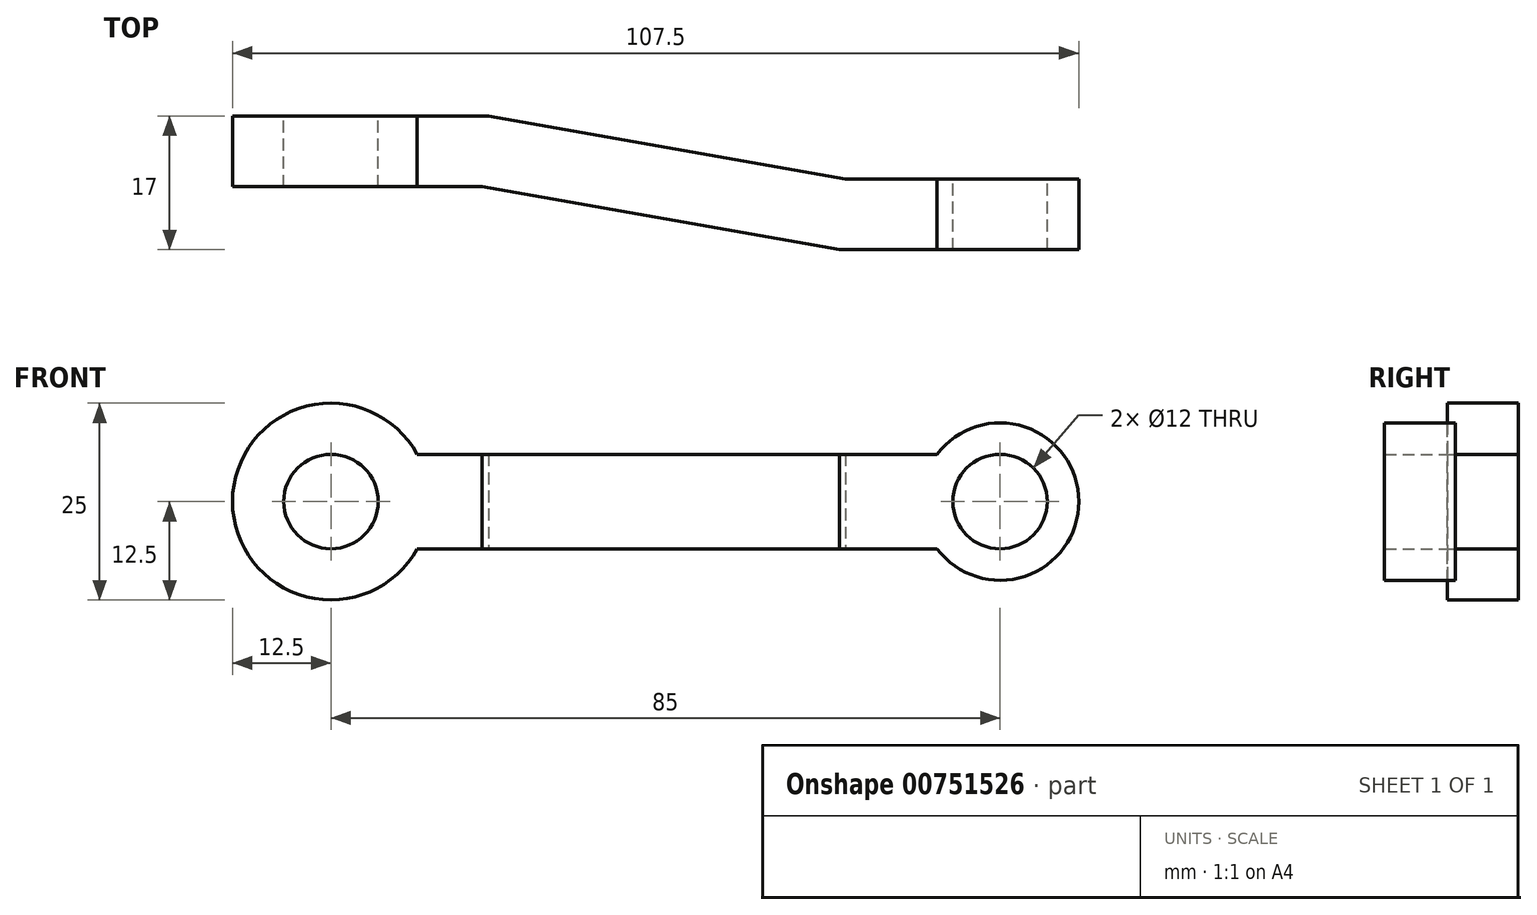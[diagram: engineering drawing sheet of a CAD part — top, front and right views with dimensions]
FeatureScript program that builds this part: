
annotation { "Feature Type Name" : "Feature", "Feature Type Description" : "" }
export const myFeature = defineFeature(function(context is Context, id is Id, definition is map)
    precondition{}
    {
        {
            var Q0;
            Q0=qCreatedBy(makeId("Front.planeOp"),FACE);
            var sketch = newSketch(context, id + "F0", { "sketchPlane" : qUnion([Q0])});
            skCircle(sketch, "E0", {"center": v(0, 0) * mm, "radius": 12.5 * mm});
            skCircle(sketch, "E1", {"center": v(85, 0) * mm, "radius": 10 * mm});
            skLineSegment(sketch, "E2", {"start": v(10.97, 6) * mm, "end": v(77, 6) * mm});
            skLineSegment(sketch, "E3", {"start": v(1.08, 0) * mm, "end": v(85, 0) * mm, "construction": true});
            skLineSegment(sketch, "E4.MirrorCS", {"start": v(10.97, -6) * mm, "end": v(77, -6) * mm});
            skCircle(sketch, "E5", {"center": v(0, 0) * mm, "radius": 6 * mm});
            skCircle(sketch, "E6", {"center": v(85, 0) * mm, "radius": 6 * mm});
            skSolve(sketch);
        }
        {
            var Q0;
            {var subQ0=sQuery(id+"F0.wireOp",EDGE,"E2");Q0=makeQuery(id+"F0.imprint","IMPRINT",FACE,{"disambiguationData":[TD([[makeQuery(id+"F0.imprint","IMPRINT",EDGE,{"derivedFrom":subQ0}),-1.0]])]});}
            var Q1;
            Q1=makeQuery(id+"F0.imprint","IMPRINT",FACE,{"disambiguationData":[TD([[makeQuery(id+"F0.imprint","IMPRINT",EDGE,{"derivedFrom":sQuery(id+"F0.wireOp",EDGE,"E6")}),-1.0]])]});
            var Q2;
            Q2=makeQuery(id+"F0.imprint","IMPRINT",FACE,{"disambiguationData":[TD([[makeQuery(id+"F0.imprint","IMPRINT",EDGE,{"derivedFrom":sQuery(id+"F0.wireOp",EDGE,"E5")}),-1.0]])]});
            extrude(context, id + "F1", {"entities" : qUnion([Q0, Q1, Q2]), "depth" : 25 * mm, "offsetDistance" : 25 * mm});
        }
        {
            var Q0;
            Q0=qCreatedBy(makeId("Top.planeOp"),FACE);
            var sketch = newSketch(context, id + "F2", { "sketchPlane" : qUnion([Q0])});
            skLineSegment(sketch, "E7", {"start": v(-12.5, 0) * mm, "end": v(20, 0) * mm});
            skLineSegment(sketch, "E8", {"start": v(20, 0) * mm, "end": v(65.37, -8) * mm});
            skLineSegment(sketch, "E9", {"start": v(65.37, -8) * mm, "end": v(95, -8) * mm});
            skLineSegment(sketch, "E10.0", {"start": v(64.58, -17) * mm, "end": v(95, -17) * mm});
            skLineSegment(sketch, "E10.1", {"start": v(19.21, -9) * mm, "end": v(64.58, -17) * mm});
            skLineSegment(sketch, "E10.2", {"start": v(-12.5, -9) * mm, "end": v(19.21, -9) * mm});
            skLineSegment(sketch, "E11", {"start": v(-12.5, -9) * mm, "end": v(-12.5, 0) * mm});
            skLineSegment(sketch, "E12", {"start": v(95, -17) * mm, "end": v(95, -8) * mm});
            skLineSegment(sketch, "E13", {"start": v(-12.5, -25) * mm, "end": v(-12.5, 0) * mm});
            skLineSegment(sketch, "E14", {"start": v(95, 0) * mm, "end": v(95, -25) * mm});
            skSolve(sketch);
        }
        {
            var Q0;
            Q0 = qSketchRegion(id + "F2", true);
            extrude(context, id + "F3", {"entities" : qUnion([Q0]), "operationType" : NewBodyOperationType.INTERSECT, "endBound" : BoundingType.SYMMETRIC, "depth" : 25 * mm, "offsetDistance" : 25 * mm});
        }
    });
